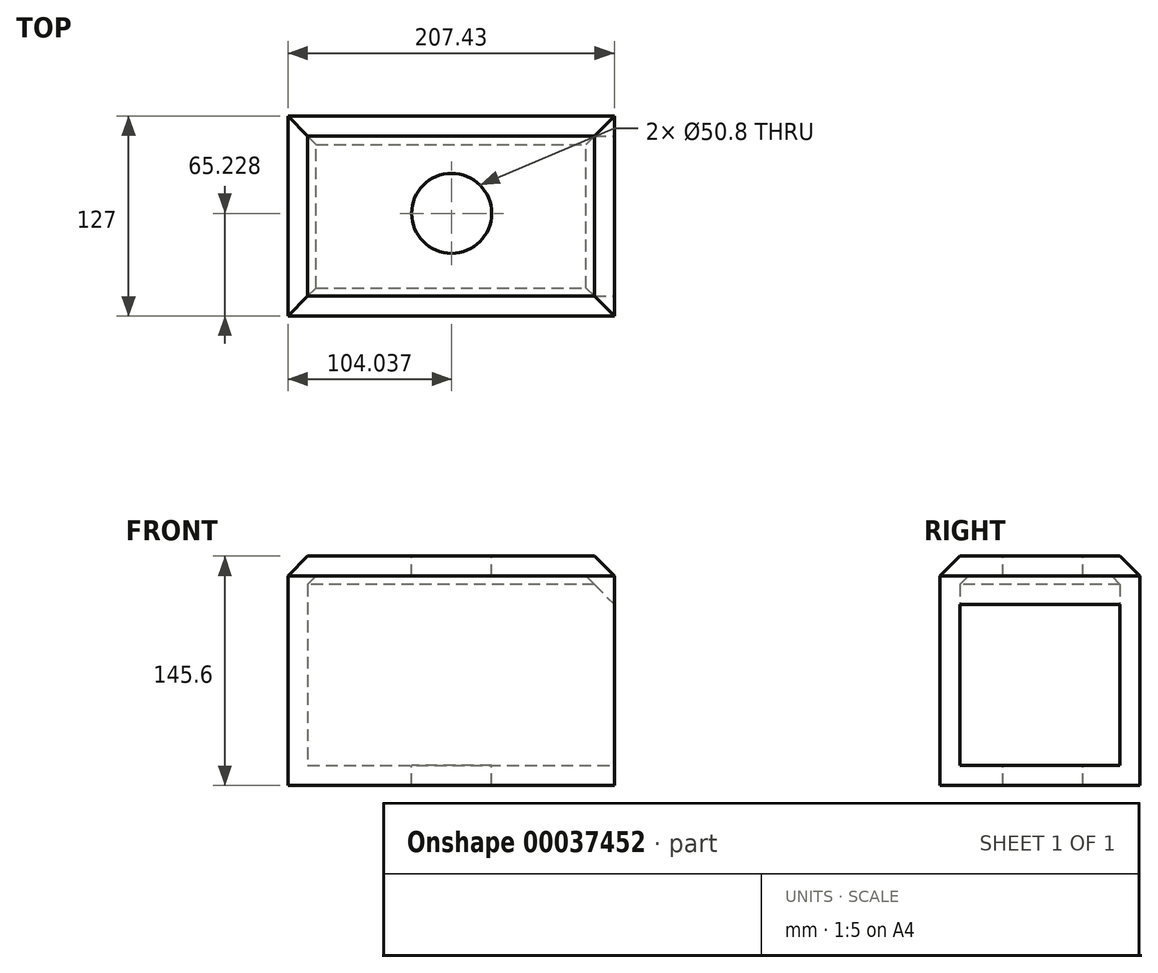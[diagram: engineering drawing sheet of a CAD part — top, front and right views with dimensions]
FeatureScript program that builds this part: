
annotation { "Feature Type Name" : "Feature", "Feature Type Description" : "" }
export const myFeature = defineFeature(function(context is Context, id is Id, definition is map)
    precondition{}
    {
        {
            var Q0;
            Q0=qCreatedBy(makeId("Top.planeOp"),FACE);
            var sketch = newSketch(context, id + "F0", { "sketchPlane" : qUnion([Q0])});
            skLineSegment(sketch, "E0.bottom", {"start": v(0, 0) * mm, "end": v(207.43, 0) * mm});
            skLineSegment(sketch, "E0.top", {"start": v(0, 127) * mm, "end": v(207.43, 127) * mm});
            skLineSegment(sketch, "E0.left", {"start": v(0, 0) * mm, "end": v(0, 127) * mm});
            skLineSegment(sketch, "E0.right", {"start": v(207.43, 0) * mm, "end": v(207.43, 127) * mm});
            skSolve(sketch);
        }
        {
            var Q0;
            Q0=makeQuery(id+"F0.imprint","IMPRINT",FACE,{"disambiguationData":[TD([[makeQuery(id+"F0.imprint","IMPRINT",EDGE,{"derivedFrom":sQuery(id+"F0.wireOp",EDGE,"E0.bottom")}),1.0]])]});
            extrude(context, id + "F1", {"entities" : qUnion([Q0]), "endBound" : BoundingType.SYMMETRIC, "depth" : 145.6 * mm});
        }
        {
            var Q0;
            Q0=makeQuery(id+"F1.opExtrude","CAP_EDGE",EDGE,{"disambiguationData":[OSD([sQuery(id+"F0.wireOp",EDGE,"E0.right")])],"isStart":false});
            var Q1;
            Q1=makeQuery(id+"F1.opExtrude","CAP_EDGE",EDGE,{"disambiguationData":[OSD([sQuery(id+"F0.wireOp",EDGE,"E0.top")])],"isStart":false});
            var Q2;
            Q2=makeQuery(id+"F1.opExtrude","CAP_EDGE",EDGE,{"disambiguationData":[OSD([sQuery(id+"F0.wireOp",EDGE,"E0.left")])],"isStart":false});
            var Q3;
            Q3=makeQuery(id+"F1.opExtrude","CAP_EDGE",EDGE,{"disambiguationData":[OSD([sQuery(id+"F0.wireOp",EDGE,"E0.bottom")])],"isStart":false});
            chamfer(context, id + "F2", {"entities" : qUnion([Q0, Q1, Q2, Q3]), "width" : 12.7 * mm, "tangentPropagation" : true});
        }
        {
            var Q0;
            Q0=makeQuery(id+"F1.opExtrude","SWEPT_FACE",FACE,{"disambiguationData":[OSD([sQuery(id+"F0.wireOp",EDGE,"E0.right")])]});
            shell(context, id + "F3", {"entities" : qUnion([Q0]), "thickness" : 12.7 * mm});
        }
        {
            var Q0;
            Q0=makeQuery(id+"F1.opExtrude","CAP_FACE",FACE,{"disambiguationData":[OSD([sQuery(id+"F0.wireOp",EDGE,"E0.bottom"),sQuery(id+"F0.wireOp",EDGE,"E0.top"),sQuery(id+"F0.wireOp",EDGE,"E0.left"),sQuery(id+"F0.wireOp",EDGE,"E0.right")])],"isStart":false});
            var sketch = newSketch(context, id + "F4", { "sketchPlane" : qUnion([Q0])});
            skCircle(sketch, "E1", {"center": v(104.04, 65.23) * mm, "radius": 25.4 * mm});
            skSolve(sketch);
        }
        {
            var Q0;
            Q0=makeQuery(id+"F4.imprint","IMPRINT",FACE,{"disambiguationData":[TD([[makeQuery(id+"F4.imprint","IMPRINT",EDGE,{"derivedFrom":sQuery(id+"F4.wireOp",EDGE,"E1")}),1.0]])]});
            var Q1;
            Q1=sQuery(id+"F4.wireOp",EDGE,"E1");
            extrude(context, id + "F5", {"entities" : qUnion([Q0]), "operationType" : NewBodyOperationType.REMOVE, "surfaceEntities" : qUnion([Q1]), "oppositeDirection" : true, "depth" : 148.94 * mm});
        }
    });
